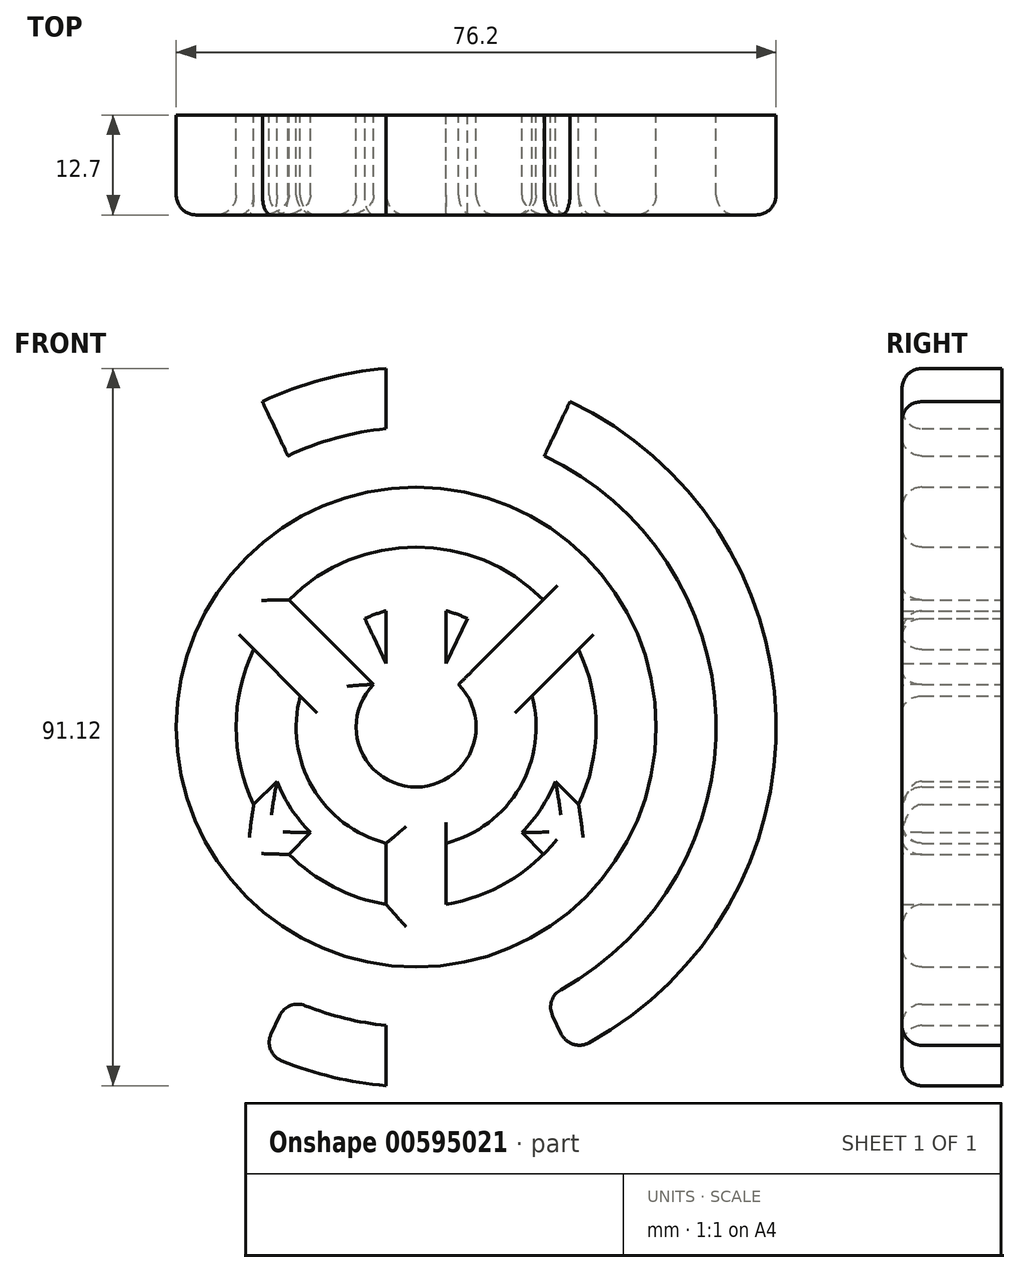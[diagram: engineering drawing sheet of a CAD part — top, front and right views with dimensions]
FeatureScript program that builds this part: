
annotation { "Feature Type Name" : "Feature", "Feature Type Description" : "" }
export const myFeature = defineFeature(function(context is Context, id is Id, definition is map)
    precondition{}
    {
        {
            var Q0;
            Q0=qCreatedBy(makeId("Front.planeOp"),FACE);
            var sketch = newSketch(context, id + "F0", { "sketchPlane" : qUnion([Q0])});
            skCircle(sketch, "E0", {"center": v(0, 0) * mm, "radius": 45.72 * mm});
            skCircle(sketch, "E1", {"center": v(0, 0) * mm, "radius": 38.1 * mm});
            skCircle(sketch, "E2", {"center": v(0, 0) * mm, "radius": 15.24 * mm});
            skCircle(sketch, "E3", {"center": v(0, 0) * mm, "radius": 7.62 * mm});
            skCircle(sketch, "E4", {"center": v(0, 0) * mm, "radius": 30.48 * mm});
            skCircle(sketch, "E5", {"center": v(0, 0) * mm, "radius": 22.86 * mm});
            skLineSegment(sketch, "E6", {"start": v(0, 0) * mm, "end": v(0, -45.72) * mm, "construction": true});
            skLineSegment(sketch, "E7", {"start": v(0, -45.72) * mm, "end": v(0, 45.72) * mm, "construction": true});
            skLineSegment(sketch, "E8", {"start": v(0, 0) * mm, "end": v(-45.72, 0) * mm});
            skLineSegment(sketch, "E9", {"start": v(-45.72, 0) * mm, "end": v(45.72, 0) * mm});
            skLineSegment(sketch, "E10", {"start": v(3.8, 45.56) * mm, "end": v(3.81, -45.56) * mm});
            skLineSegment(sketch, "E11", {"start": v(3.81, -45.56) * mm, "end": v(3.8, 45.56) * mm});
            skLineSegment(sketch, "E12", {"start": v(-3.81, 45.56) * mm, "end": v(-3.8, -45.56) * mm});
            skLineSegment(sketch, "E13", {"start": v(0, 0) * mm, "end": v(19.54, 41.34) * mm});
            skLineSegment(sketch, "E14", {"start": v(19.54, 41.34) * mm, "end": v(-19.54, -41.34) * mm});
            skLineSegment(sketch, "E15.MirrorCS", {"start": v(0, 0) * mm, "end": v(-19.54, 41.34) * mm});
            skLineSegment(sketch, "E16.MirrorCS", {"start": v(-19.54, 41.34) * mm, "end": v(19.54, -41.34) * mm});
            skLineSegment(sketch, "E17", {"start": v(0, 0) * mm, "end": v(21.55, 21.55) * mm});
            skLineSegment(sketch, "E18", {"start": v(21.55, 21.55) * mm, "end": v(0, 0) * mm});
            skLineSegment(sketch, "E19", {"start": v(26.26, 15.48) * mm, "end": v(10.78, 0) * mm});
            skPoint(sketch, "E19.endSnap0", {"position": v(3.8, 0) * mm});
            skLineSegment(sketch, "E20", {"start": v(10.78, 0) * mm, "end": v(26.26, -15.48) * mm});
            skLineSegment(sketch, "E21", {"start": v(0, 0) * mm, "end": v(21.55, -21.55) * mm});
            skLineSegment(sketch, "E22.MirrorCS", {"start": v(0, 0) * mm, "end": v(-21.55, -21.55) * mm});
            skLineSegment(sketch, "E23.MirrorCS", {"start": v(-10.78, 0) * mm, "end": v(-26.26, -15.48) * mm});
            skLineSegment(sketch, "E24.MirrorCS", {"start": v(-21.55, 21.55) * mm, "end": v(0, 0) * mm});
            skLineSegment(sketch, "E25.MirrorCS", {"start": v(-26.26, 15.48) * mm, "end": v(-10.78, 0) * mm});
            skCircle(sketch, "E26", {"center": v(0, 0) * mm, "radius": 18.97 * mm});
            skSolve(sketch);
        }
        {
            var Q0;
            {var subQ0=sQuery(id+"F0.wireOp",EDGE,"E19");var subQ1=sQuery(id+"F0.wireOp",EDGE,"E5");var subQ2=makeQuery(id+"F0.imprint","INTERSECT",VERTEX,{"derivedFrom":[subQ1,subQ0]});Q0=makeQuery(id+"F0.imprint","IMPRINT",FACE,{"disambiguationData":[TD([[makeQuery(id+"F0.imprint","IMPRINT",EDGE,{"disambiguationData":[TD([[subQ2,-1.0]])],"derivedFrom":subQ1}),1.0]])]});}
            var Q1;
            {var subQ0=sQuery(id+"F0.wireOp",EDGE,"E23.MirrorCS");var subQ1=sQuery(id+"F0.wireOp",EDGE,"E5");var subQ2=makeQuery(id+"F0.imprint","INTERSECT",VERTEX,{"derivedFrom":[subQ1,subQ0]});Q1=makeQuery(id+"F0.imprint","IMPRINT",FACE,{"disambiguationData":[TD([[makeQuery(id+"F0.imprint","IMPRINT",EDGE,{"disambiguationData":[TD([[subQ2,-1.0]])],"derivedFrom":subQ1}),1.0]])]});}
            var Q2;
            {var subQ3=sQuery(id+"F0.wireOp",EDGE,"E2");var subQ7=sQuery(id+"F0.wireOp",EDGE,"E21");var subQ9=makeQuery(id+"F0.imprint","INTERSECT",VERTEX,{"derivedFrom":[subQ3,subQ7]});Q2=makeQuery(id+"F0.imprint","IMPRINT",FACE,{"disambiguationData":[TD([[makeQuery(id+"F0.imprint","IMPRINT",EDGE,{"disambiguationData":[TD([[subQ9,-1.0]])],"derivedFrom":subQ3}),1.0]])]});}
            var Q3;
            {var subQ0=sQuery(id+"F0.wireOp",EDGE,"E12");var subQ1=sQuery(id+"F0.wireOp",EDGE,"E3");var subQ2=makeQuery(id+"F0.imprint","INTERSECT",VERTEX,{"disambiguationData":[OD(1.0)],"derivedFrom":[subQ1,subQ0]});Q3=makeQuery(id+"F0.imprint","IMPRINT",FACE,{"disambiguationData":[TD([[makeQuery(id+"F0.imprint","IMPRINT",EDGE,{"disambiguationData":[TD([[subQ2,-1.0]])],"derivedFrom":subQ1}),-1.0]])]});}
            var Q4;
            {var subQ0=sQuery(id+"F0.wireOp",EDGE,"E9");var subQ1=sQuery(id+"F0.wireOp",EDGE,"E0");var subQ2=makeQuery(id+"F0.imprint","INTERSECT",VERTEX,{"disambiguationData":[OD(0.0)],"derivedFrom":[subQ1,subQ0]});Q4=makeQuery(id+"F0.imprint","IMPRINT",FACE,{"disambiguationData":[TD([[makeQuery(id+"F0.imprint","IMPRINT",EDGE,{"disambiguationData":[TD([[subQ2,1.0]])],"derivedFrom":subQ1}),1.0]])]});}
            var Q5;
            {var subQ0=sQuery(id+"F0.wireOp",EDGE,"E11");var subQ1=sQuery(id+"F0.wireOp",EDGE,"E0");var subQ2=makeQuery(id+"F0.imprint","INTERSECT",VERTEX,{"disambiguationData":[OD(0.0)],"derivedFrom":[subQ1,subQ0]});Q5=makeQuery(id+"F0.imprint","IMPRINT",FACE,{"disambiguationData":[TD([[makeQuery(id+"F0.imprint","IMPRINT",EDGE,{"disambiguationData":[TD([[subQ2,1.0]])],"derivedFrom":subQ1}),1.0]])]});}
            var Q6;
            {var subQ0=sQuery(id+"F0.wireOp",EDGE,"E9");var subQ1=sQuery(id+"F0.wireOp",EDGE,"E0");var subQ2=makeQuery(id+"F0.imprint","INTERSECT",VERTEX,{"disambiguationData":[OD(1.0)],"derivedFrom":[subQ1,subQ0]});Q6=makeQuery(id+"F0.imprint","IMPRINT",FACE,{"disambiguationData":[TD([[makeQuery(id+"F0.imprint","IMPRINT",EDGE,{"disambiguationData":[TD([[subQ2,-1.0]])],"derivedFrom":subQ1}),1.0]])]});}
            var Q7;
            {var subQ0=sQuery(id+"F0.wireOp",EDGE,"E25.MirrorCS");var subQ1=sQuery(id+"F0.wireOp",EDGE,"E2");var subQ2=makeQuery(id+"F0.imprint","INTERSECT",VERTEX,{"derivedFrom":[subQ1,subQ0]});Q7=makeQuery(id+"F0.imprint","IMPRINT",FACE,{"disambiguationData":[TD([[makeQuery(id+"F0.imprint","IMPRINT",EDGE,{"disambiguationData":[TD([[subQ2,-1.0]])],"derivedFrom":subQ1}),1.0]])]});}
            var Q8;
            {var subQ0=sQuery(id+"F0.wireOp",EDGE,"E9");var subQ1=sQuery(id+"F0.wireOp",EDGE,"E0");var subQ2=makeQuery(id+"F0.imprint","INTERSECT",VERTEX,{"disambiguationData":[OD(1.0)],"derivedFrom":[subQ1,subQ0]});Q8=makeQuery(id+"F0.imprint","IMPRINT",FACE,{"disambiguationData":[TD([[makeQuery(id+"F0.imprint","IMPRINT",EDGE,{"disambiguationData":[TD([[subQ2,1.0]])],"derivedFrom":subQ1}),1.0]])]});}
            var Q9;
            {var subQ0=sQuery(id+"F0.wireOp",EDGE,"E12");var subQ1=sQuery(id+"F0.wireOp",EDGE,"E4");var subQ2=makeQuery(id+"F0.imprint","INTERSECT",VERTEX,{"disambiguationData":[OD(0.0)],"derivedFrom":[subQ1,subQ0]});Q9=makeQuery(id+"F0.imprint","IMPRINT",FACE,{"disambiguationData":[TD([[makeQuery(id+"F0.imprint","IMPRINT",EDGE,{"disambiguationData":[TD([[subQ2,-1.0]])],"derivedFrom":subQ1}),1.0]])]});}
            var Q10;
            {var subQ0=sQuery(id+"F0.wireOp",EDGE,"E24.MirrorCS");var subQ1=sQuery(id+"F0.wireOp",EDGE,"E5");var subQ2=makeQuery(id+"F0.imprint","INTERSECT",VERTEX,{"derivedFrom":[subQ1,subQ0]});Q10=makeQuery(id+"F0.imprint","IMPRINT",FACE,{"disambiguationData":[TD([[makeQuery(id+"F0.imprint","IMPRINT",EDGE,{"disambiguationData":[TD([[subQ2,-1.0]])],"derivedFrom":subQ1}),1.0]])]});}
            var Q11;
            {var subQ0=sQuery(id+"F0.wireOp",EDGE,"E23.MirrorCS");var subQ1=sQuery(id+"F0.wireOp",EDGE,"E4");var subQ2=makeQuery(id+"F0.imprint","INTERSECT",VERTEX,{"derivedFrom":[subQ1,subQ0]});Q11=makeQuery(id+"F0.imprint","IMPRINT",FACE,{"disambiguationData":[TD([[makeQuery(id+"F0.imprint","IMPRINT",EDGE,{"disambiguationData":[TD([[subQ2,1.0]])],"derivedFrom":subQ1}),1.0]])]});}
            var Q12;
            {var subQ0=sQuery(id+"F0.wireOp",EDGE,"E11");var subQ1=sQuery(id+"F0.wireOp",EDGE,"E2");var subQ2=makeQuery(id+"F0.imprint","INTERSECT",VERTEX,{"disambiguationData":[OD(0.0)],"derivedFrom":[subQ1,subQ0]});Q12=makeQuery(id+"F0.imprint","IMPRINT",FACE,{"disambiguationData":[TD([[makeQuery(id+"F0.imprint","IMPRINT",EDGE,{"disambiguationData":[TD([[subQ2,-1.0]])],"derivedFrom":subQ1}),-1.0]])]});}
            var Q13;
            {var subQ0=sQuery(id+"F0.wireOp",EDGE,"E25.MirrorCS");var subQ1=sQuery(id+"F0.wireOp",EDGE,"E4");var subQ2=makeQuery(id+"F0.imprint","INTERSECT",VERTEX,{"derivedFrom":[subQ1,subQ0]});Q13=makeQuery(id+"F0.imprint","IMPRINT",FACE,{"disambiguationData":[TD([[makeQuery(id+"F0.imprint","IMPRINT",EDGE,{"disambiguationData":[TD([[subQ2,-1.0]])],"derivedFrom":subQ1}),1.0]])]});}
            var Q14;
            {var subQ0=sQuery(id+"F0.wireOp",EDGE,"E11");var subQ1=sQuery(id+"F0.wireOp",EDGE,"E4");var subQ2=makeQuery(id+"F0.imprint","INTERSECT",VERTEX,{"disambiguationData":[OD(1.0)],"derivedFrom":[subQ1,subQ0]});Q14=makeQuery(id+"F0.imprint","IMPRINT",FACE,{"disambiguationData":[TD([[makeQuery(id+"F0.imprint","IMPRINT",EDGE,{"disambiguationData":[TD([[subQ2,-1.0]])],"derivedFrom":subQ1}),1.0]])]});}
            var Q15;
            {var subQ0=sQuery(id+"F0.wireOp",EDGE,"E21");var subQ1=sQuery(id+"F0.wireOp",EDGE,"E5");var subQ2=makeQuery(id+"F0.imprint","INTERSECT",VERTEX,{"derivedFrom":[subQ1,subQ0]});Q15=makeQuery(id+"F0.imprint","IMPRINT",FACE,{"disambiguationData":[TD([[makeQuery(id+"F0.imprint","IMPRINT",EDGE,{"disambiguationData":[TD([[subQ2,-1.0]])],"derivedFrom":subQ1}),1.0]])]});}
            var Q16;
            {var subQ0=sQuery(id+"F0.wireOp",EDGE,"E20");var subQ1=sQuery(id+"F0.wireOp",EDGE,"E4");var subQ2=makeQuery(id+"F0.imprint","INTERSECT",VERTEX,{"derivedFrom":[subQ1,subQ0]});Q16=makeQuery(id+"F0.imprint","IMPRINT",FACE,{"disambiguationData":[TD([[makeQuery(id+"F0.imprint","IMPRINT",EDGE,{"disambiguationData":[TD([[subQ2,-1.0]])],"derivedFrom":subQ1}),1.0]])]});}
            var Q17;
            {var subQ0=sQuery(id+"F0.wireOp",EDGE,"E12");var subQ1=sQuery(id+"F0.wireOp",EDGE,"E2");var subQ2=makeQuery(id+"F0.imprint","INTERSECT",VERTEX,{"disambiguationData":[OD(1.0)],"derivedFrom":[subQ1,subQ0]});Q17=makeQuery(id+"F0.imprint","IMPRINT",FACE,{"disambiguationData":[TD([[makeQuery(id+"F0.imprint","IMPRINT",EDGE,{"disambiguationData":[TD([[subQ2,-1.0]])],"derivedFrom":subQ1}),1.0]])]});}
            var Q18;
            {var subQ0=sQuery(id+"F0.wireOp",EDGE,"E12");var subQ1=sQuery(id+"F0.wireOp",EDGE,"E4");var subQ2=makeQuery(id+"F0.imprint","INTERSECT",VERTEX,{"disambiguationData":[OD(1.0)],"derivedFrom":[subQ1,subQ0]});Q18=makeQuery(id+"F0.imprint","IMPRINT",FACE,{"disambiguationData":[TD([[makeQuery(id+"F0.imprint","IMPRINT",EDGE,{"disambiguationData":[TD([[subQ2,-1.0]])],"derivedFrom":subQ1}),1.0]])]});}
            var Q19;
            {var subQ0=sQuery(id+"F0.wireOp",EDGE,"E11");var subQ1=sQuery(id+"F0.wireOp",EDGE,"E0");var subQ2=makeQuery(id+"F0.imprint","INTERSECT",VERTEX,{"disambiguationData":[OD(1.0)],"derivedFrom":[subQ1,subQ0]});Q19=makeQuery(id+"F0.imprint","IMPRINT",FACE,{"disambiguationData":[TD([[makeQuery(id+"F0.imprint","IMPRINT",EDGE,{"disambiguationData":[TD([[subQ2,-1.0]])],"derivedFrom":subQ1}),1.0]])]});}
            var Q20;
            {var subQ1=sQuery(id+"F0.wireOp",EDGE,"E2");var subQ5=sQuery(id+"F0.wireOp",EDGE,"E19");var subQ9=makeQuery(id+"F0.imprint","INTERSECT",VERTEX,{"derivedFrom":[subQ1,subQ5]});Q20=makeQuery(id+"F0.imprint","IMPRINT",FACE,{"disambiguationData":[TD([[makeQuery(id+"F0.imprint","IMPRINT",EDGE,{"disambiguationData":[TD([[subQ9,-1.0]])],"derivedFrom":subQ1}),1.0]])]});}
            var Q21;
            {var subQ0=sQuery(id+"F0.wireOp",EDGE,"E14");var subQ1=sQuery(id+"F0.wireOp",EDGE,"E2");var subQ2=makeQuery(id+"F0.imprint","INTERSECT",VERTEX,{"disambiguationData":[OD(0.0)],"derivedFrom":[subQ1,subQ0]});Q21=makeQuery(id+"F0.imprint","IMPRINT",FACE,{"disambiguationData":[TD([[makeQuery(id+"F0.imprint","IMPRINT",EDGE,{"disambiguationData":[TD([[subQ2,-1.0]])],"derivedFrom":subQ1}),1.0]])]});}
            var Q22;
            {var subQ0=sQuery(id+"F0.wireOp",EDGE,"E16.MirrorCS");var subQ1=sQuery(id+"F0.wireOp",EDGE,"E2");var subQ2=makeQuery(id+"F0.imprint","INTERSECT",VERTEX,{"disambiguationData":[OD(1.0)],"derivedFrom":[subQ1,subQ0]});Q22=makeQuery(id+"F0.imprint","IMPRINT",FACE,{"disambiguationData":[TD([[makeQuery(id+"F0.imprint","IMPRINT",EDGE,{"disambiguationData":[TD([[subQ2,-1.0]])],"derivedFrom":subQ1}),1.0]])]});}
            var Q23;
            {var subQ0=sQuery(id+"F0.wireOp",EDGE,"E18");var subQ6=sQuery(id+"F0.wireOp",EDGE,"E2");var subQ9=makeQuery(id+"F0.imprint","INTERSECT",VERTEX,{"derivedFrom":[subQ6,subQ0]});Q23=makeQuery(id+"F0.imprint","IMPRINT",FACE,{"disambiguationData":[TD([[makeQuery(id+"F0.imprint","IMPRINT",EDGE,{"disambiguationData":[TD([[subQ9,-1.0]])],"derivedFrom":subQ6}),1.0]])]});}
            var Q24;
            {var subQ0=sQuery(id+"F0.wireOp",EDGE,"E9");var subQ1=sQuery(id+"F0.wireOp",EDGE,"E2");var subQ2=makeQuery(id+"F0.imprint","INTERSECT",VERTEX,{"disambiguationData":[OD(1.0)],"derivedFrom":[subQ1,subQ0]});Q24=makeQuery(id+"F0.imprint","IMPRINT",FACE,{"disambiguationData":[TD([[makeQuery(id+"F0.imprint","IMPRINT",EDGE,{"disambiguationData":[TD([[subQ2,-1.0]])],"derivedFrom":subQ1}),1.0]])]});}
            var Q25;
            {var subQ0=sQuery(id+"F0.wireOp",EDGE,"E11");var subQ1=sQuery(id+"F0.wireOp",EDGE,"E3");var subQ2=makeQuery(id+"F0.imprint","INTERSECT",VERTEX,{"disambiguationData":[OD(0.0)],"derivedFrom":[subQ1,subQ0]});Q25=makeQuery(id+"F0.imprint","IMPRINT",FACE,{"disambiguationData":[TD([[makeQuery(id+"F0.imprint","IMPRINT",EDGE,{"disambiguationData":[TD([[subQ2,-1.0]])],"derivedFrom":subQ1}),-1.0]])]});}
            var Q26;
            {var subQ0=sQuery(id+"F0.wireOp",EDGE,"E16.MirrorCS");var subQ1=sQuery(id+"F0.wireOp",EDGE,"E3");var subQ2=makeQuery(id+"F0.imprint","INTERSECT",VERTEX,{"disambiguationData":[OD(0.0)],"derivedFrom":[subQ1,subQ0]});Q26=makeQuery(id+"F0.imprint","IMPRINT",FACE,{"disambiguationData":[TD([[makeQuery(id+"F0.imprint","IMPRINT",EDGE,{"disambiguationData":[TD([[subQ2,-1.0]])],"derivedFrom":subQ1}),-1.0]])]});}
            var Q27;
            {var subQ0=sQuery(id+"F0.wireOp",EDGE,"E18");var subQ1=sQuery(id+"F0.wireOp",EDGE,"E4");var subQ2=makeQuery(id+"F0.imprint","INTERSECT",VERTEX,{"derivedFrom":[subQ1,subQ0]});Q27=makeQuery(id+"F0.imprint","IMPRINT",FACE,{"disambiguationData":[TD([[makeQuery(id+"F0.imprint","IMPRINT",EDGE,{"disambiguationData":[TD([[subQ2,1.0]])],"derivedFrom":subQ1}),1.0]])]});}
            var Q28;
            {var subQ0=sQuery(id+"F0.wireOp",EDGE,"E11");var subQ1=sQuery(id+"F0.wireOp",EDGE,"E2");var subQ2=makeQuery(id+"F0.imprint","INTERSECT",VERTEX,{"disambiguationData":[OD(1.0)],"derivedFrom":[subQ1,subQ0]});Q28=makeQuery(id+"F0.imprint","IMPRINT",FACE,{"disambiguationData":[TD([[makeQuery(id+"F0.imprint","IMPRINT",EDGE,{"disambiguationData":[TD([[subQ2,-1.0]])],"derivedFrom":subQ1}),1.0]])]});}
            var Q29;
            {var subQ0=sQuery(id+"F0.wireOp",EDGE,"E20");var subQ1=sQuery(id+"F0.wireOp",EDGE,"E4");var subQ2=makeQuery(id+"F0.imprint","INTERSECT",VERTEX,{"derivedFrom":[subQ1,subQ0]});Q29=makeQuery(id+"F0.imprint","IMPRINT",FACE,{"disambiguationData":[TD([[makeQuery(id+"F0.imprint","IMPRINT",EDGE,{"disambiguationData":[TD([[subQ2,1.0]])],"derivedFrom":subQ1}),1.0]])]});}
            var Q30;
            {var subQ0=sQuery(id+"F0.wireOp",EDGE,"E12");var subQ1=sQuery(id+"F0.wireOp",EDGE,"E2");var subQ2=makeQuery(id+"F0.imprint","INTERSECT",VERTEX,{"disambiguationData":[OD(1.0)],"derivedFrom":[subQ1,subQ0]});Q30=makeQuery(id+"F0.imprint","IMPRINT",FACE,{"disambiguationData":[TD([[makeQuery(id+"F0.imprint","IMPRINT",EDGE,{"disambiguationData":[TD([[subQ2,-1.0]])],"derivedFrom":subQ1}),-1.0]])]});}
            var Q31;
            {var subQ0=sQuery(id+"F0.wireOp",EDGE,"E11");var subQ1=sQuery(id+"F0.wireOp",EDGE,"E4");var subQ2=makeQuery(id+"F0.imprint","INTERSECT",VERTEX,{"disambiguationData":[OD(0.0)],"derivedFrom":[subQ1,subQ0]});Q31=makeQuery(id+"F0.imprint","IMPRINT",FACE,{"disambiguationData":[TD([[makeQuery(id+"F0.imprint","IMPRINT",EDGE,{"disambiguationData":[TD([[subQ2,-1.0]])],"derivedFrom":subQ1}),1.0]])]});}
            var Q32;
            {var subQ0=sQuery(id+"F0.wireOp",EDGE,"E9");var subQ1=sQuery(id+"F0.wireOp",EDGE,"E0");var subQ2=makeQuery(id+"F0.imprint","INTERSECT",VERTEX,{"disambiguationData":[OD(0.0)],"derivedFrom":[subQ1,subQ0]});Q32=makeQuery(id+"F0.imprint","IMPRINT",FACE,{"disambiguationData":[TD([[makeQuery(id+"F0.imprint","IMPRINT",EDGE,{"disambiguationData":[TD([[subQ2,-1.0]])],"derivedFrom":subQ1}),1.0]])]});}
            var Q33;
            {var subQ0=sQuery(id+"F0.wireOp",EDGE,"E16.MirrorCS");var subQ1=sQuery(id+"F0.wireOp",EDGE,"E3");var subQ2=makeQuery(id+"F0.imprint","INTERSECT",VERTEX,{"disambiguationData":[OD(1.0)],"derivedFrom":[subQ1,subQ0]});Q33=makeQuery(id+"F0.imprint","IMPRINT",FACE,{"disambiguationData":[TD([[makeQuery(id+"F0.imprint","IMPRINT",EDGE,{"disambiguationData":[TD([[subQ2,-1.0]])],"derivedFrom":subQ1}),-1.0]])]});}
            var Q34;
            {var subQ0=sQuery(id+"F0.wireOp",EDGE,"E19");var subQ1=sQuery(id+"F0.wireOp",EDGE,"E2");var subQ2=makeQuery(id+"F0.imprint","INTERSECT",VERTEX,{"derivedFrom":[subQ1,subQ0]});Q34=makeQuery(id+"F0.imprint","IMPRINT",FACE,{"disambiguationData":[TD([[makeQuery(id+"F0.imprint","IMPRINT",EDGE,{"disambiguationData":[TD([[subQ2,-1.0]])],"derivedFrom":subQ1}),-1.0]])]});}
            var Q35;
            {var subQ5=sQuery(id+"F0.wireOp",EDGE,"E24.MirrorCS");var subQ7=sQuery(id+"F0.wireOp",EDGE,"E2");var subQ8=makeQuery(id+"F0.imprint","INTERSECT",VERTEX,{"derivedFrom":[subQ7,subQ5]});Q35=makeQuery(id+"F0.imprint","IMPRINT",FACE,{"disambiguationData":[TD([[makeQuery(id+"F0.imprint","IMPRINT",EDGE,{"disambiguationData":[TD([[subQ8,-1.0]])],"derivedFrom":subQ7}),1.0]])]});}
            var Q36;
            {var subQ0=sQuery(id+"F0.wireOp",EDGE,"E12");var subQ1=sQuery(id+"F0.wireOp",EDGE,"E5");var subQ2=makeQuery(id+"F0.imprint","INTERSECT",VERTEX,{"disambiguationData":[OD(1.0)],"derivedFrom":[subQ1,subQ0]});Q36=makeQuery(id+"F0.imprint","IMPRINT",FACE,{"disambiguationData":[TD([[makeQuery(id+"F0.imprint","IMPRINT",EDGE,{"disambiguationData":[TD([[subQ2,-1.0]])],"derivedFrom":subQ1}),1.0]])]});}
            var Q37;
            {var subQ0=sQuery(id+"F0.wireOp",EDGE,"E14");var subQ1=sQuery(id+"F0.wireOp",EDGE,"E4");var subQ2=makeQuery(id+"F0.imprint","INTERSECT",VERTEX,{"disambiguationData":[OD(1.0)],"derivedFrom":[subQ1,subQ0]});Q37=makeQuery(id+"F0.imprint","IMPRINT",FACE,{"disambiguationData":[TD([[makeQuery(id+"F0.imprint","IMPRINT",EDGE,{"disambiguationData":[TD([[subQ2,-1.0]])],"derivedFrom":subQ1}),1.0]])]});}
            var Q38;
            {var subQ0=sQuery(id+"F0.wireOp",EDGE,"E11");var subQ1=sQuery(id+"F0.wireOp",EDGE,"E5");var subQ2=makeQuery(id+"F0.imprint","INTERSECT",VERTEX,{"disambiguationData":[OD(0.0)],"derivedFrom":[subQ1,subQ0]});Q38=makeQuery(id+"F0.imprint","IMPRINT",FACE,{"disambiguationData":[TD([[makeQuery(id+"F0.imprint","IMPRINT",EDGE,{"disambiguationData":[TD([[subQ2,-1.0]])],"derivedFrom":subQ1}),1.0]])]});}
            var Q39;
            {var subQ0=sQuery(id+"F0.wireOp",EDGE,"E11");var subQ1=sQuery(id+"F0.wireOp",EDGE,"E2");var subQ2=makeQuery(id+"F0.imprint","INTERSECT",VERTEX,{"disambiguationData":[OD(0.0)],"derivedFrom":[subQ1,subQ0]});Q39=makeQuery(id+"F0.imprint","IMPRINT",FACE,{"disambiguationData":[TD([[makeQuery(id+"F0.imprint","IMPRINT",EDGE,{"disambiguationData":[TD([[subQ2,-1.0]])],"derivedFrom":subQ1}),1.0]])]});}
            var Q40;
            {var subQ0=sQuery(id+"F0.wireOp",EDGE,"E12");var subQ1=sQuery(id+"F0.wireOp",EDGE,"E2");var subQ2=makeQuery(id+"F0.imprint","INTERSECT",VERTEX,{"disambiguationData":[OD(0.0)],"derivedFrom":[subQ1,subQ0]});Q40=makeQuery(id+"F0.imprint","IMPRINT",FACE,{"disambiguationData":[TD([[makeQuery(id+"F0.imprint","IMPRINT",EDGE,{"disambiguationData":[TD([[subQ2,-1.0]])],"derivedFrom":subQ1}),1.0]])]});}
            var Q41;
            {var subQ3=sQuery(id+"F0.wireOp",EDGE,"E16.MirrorCS");var subQ5=sQuery(id+"F0.wireOp",EDGE,"E2");var subQ6=makeQuery(id+"F0.imprint","INTERSECT",VERTEX,{"disambiguationData":[OD(0.0)],"derivedFrom":[subQ5,subQ3]});Q41=makeQuery(id+"F0.imprint","IMPRINT",FACE,{"disambiguationData":[TD([[makeQuery(id+"F0.imprint","IMPRINT",EDGE,{"disambiguationData":[TD([[subQ6,-1.0]])],"derivedFrom":subQ5}),1.0]])]});}
            var Q42;
            {var subQ0=sQuery(id+"F0.wireOp",EDGE,"E19");var subQ1=sQuery(id+"F0.wireOp",EDGE,"E4");var subQ2=makeQuery(id+"F0.imprint","INTERSECT",VERTEX,{"derivedFrom":[subQ1,subQ0]});Q42=makeQuery(id+"F0.imprint","IMPRINT",FACE,{"disambiguationData":[TD([[makeQuery(id+"F0.imprint","IMPRINT",EDGE,{"disambiguationData":[TD([[subQ2,1.0]])],"derivedFrom":subQ1}),1.0]])]});}
            var Q43;
            {var subQ0=sQuery(id+"F0.wireOp",EDGE,"E22.MirrorCS");var subQ1=sQuery(id+"F0.wireOp",EDGE,"E4");var subQ2=makeQuery(id+"F0.imprint","INTERSECT",VERTEX,{"derivedFrom":[subQ1,subQ0]});Q43=makeQuery(id+"F0.imprint","IMPRINT",FACE,{"disambiguationData":[TD([[makeQuery(id+"F0.imprint","IMPRINT",EDGE,{"disambiguationData":[TD([[subQ2,1.0]])],"derivedFrom":subQ1}),1.0]])]});}
            var Q44;
            {var subQ1=sQuery(id+"F0.wireOp",EDGE,"E2");var subQ5=sQuery(id+"F0.wireOp",EDGE,"E23.MirrorCS");var subQ9=makeQuery(id+"F0.imprint","INTERSECT",VERTEX,{"derivedFrom":[subQ1,subQ5]});Q44=makeQuery(id+"F0.imprint","IMPRINT",FACE,{"disambiguationData":[TD([[makeQuery(id+"F0.imprint","IMPRINT",EDGE,{"disambiguationData":[TD([[subQ9,-1.0]])],"derivedFrom":subQ1}),1.0]])]});}
            var Q45;
            {var subQ0=sQuery(id+"F0.wireOp",EDGE,"E24.MirrorCS");var subQ1=sQuery(id+"F0.wireOp",EDGE,"E4");var subQ2=makeQuery(id+"F0.imprint","INTERSECT",VERTEX,{"derivedFrom":[subQ1,subQ0]});Q45=makeQuery(id+"F0.imprint","IMPRINT",FACE,{"disambiguationData":[TD([[makeQuery(id+"F0.imprint","IMPRINT",EDGE,{"disambiguationData":[TD([[subQ2,-1.0]])],"derivedFrom":subQ1}),1.0]])]});}
            var Q46;
            {var subQ0=sQuery(id+"F0.wireOp",EDGE,"E24.MirrorCS");var subQ1=sQuery(id+"F0.wireOp",EDGE,"E2");var subQ2=makeQuery(id+"F0.imprint","INTERSECT",VERTEX,{"derivedFrom":[subQ1,subQ0]});Q46=makeQuery(id+"F0.imprint","IMPRINT",FACE,{"disambiguationData":[TD([[makeQuery(id+"F0.imprint","IMPRINT",EDGE,{"disambiguationData":[TD([[subQ2,-1.0]])],"derivedFrom":subQ1}),-1.0]])]});}
            var Q47;
            {var subQ1=sQuery(id+"F0.wireOp",EDGE,"E2");var subQ5=sQuery(id+"F0.wireOp",EDGE,"E22.MirrorCS");var subQ6=makeQuery(id+"F0.imprint","INTERSECT",VERTEX,{"derivedFrom":[subQ1,subQ5]});Q47=makeQuery(id+"F0.imprint","IMPRINT",FACE,{"disambiguationData":[TD([[makeQuery(id+"F0.imprint","IMPRINT",EDGE,{"disambiguationData":[TD([[subQ6,-1.0]])],"derivedFrom":subQ1}),1.0]])]});}
            var Q48;
            {var subQ0=sQuery(id+"F0.wireOp",EDGE,"E9");var subQ1=sQuery(id+"F0.wireOp",EDGE,"E2");var subQ2=makeQuery(id+"F0.imprint","INTERSECT",VERTEX,{"disambiguationData":[OD(0.0)],"derivedFrom":[subQ1,subQ0]});Q48=makeQuery(id+"F0.imprint","IMPRINT",FACE,{"disambiguationData":[TD([[makeQuery(id+"F0.imprint","IMPRINT",EDGE,{"disambiguationData":[TD([[subQ2,1.0]])],"derivedFrom":subQ1}),1.0]])]});}
            var Q49;
            {var subQ0=sQuery(id+"F0.wireOp",EDGE,"E11");var subQ1=sQuery(id+"F0.wireOp",EDGE,"E0");var subQ2=makeQuery(id+"F0.imprint","INTERSECT",VERTEX,{"disambiguationData":[OD(0.0)],"derivedFrom":[subQ1,subQ0]});Q49=makeQuery(id+"F0.imprint","IMPRINT",FACE,{"disambiguationData":[TD([[makeQuery(id+"F0.imprint","IMPRINT",EDGE,{"disambiguationData":[TD([[subQ2,-1.0]])],"derivedFrom":subQ1}),1.0]])]});}
            var Q50;
            {var subQ0=sQuery(id+"F0.wireOp",EDGE,"E11");var subQ1=sQuery(id+"F0.wireOp",EDGE,"E0");var subQ2=makeQuery(id+"F0.imprint","INTERSECT",VERTEX,{"disambiguationData":[OD(1.0)],"derivedFrom":[subQ1,subQ0]});Q50=makeQuery(id+"F0.imprint","IMPRINT",FACE,{"disambiguationData":[TD([[makeQuery(id+"F0.imprint","IMPRINT",EDGE,{"disambiguationData":[TD([[subQ2,1.0]])],"derivedFrom":subQ1}),1.0]])]});}
            var Q51;
            {var subQ0=sQuery(id+"F0.wireOp",EDGE,"E19");var subQ1=sQuery(id+"F0.wireOp",EDGE,"E2");var subQ2=makeQuery(id+"F0.imprint","INTERSECT",VERTEX,{"derivedFrom":[subQ1,subQ0]});Q51=makeQuery(id+"F0.imprint","IMPRINT",FACE,{"disambiguationData":[TD([[makeQuery(id+"F0.imprint","IMPRINT",EDGE,{"disambiguationData":[TD([[subQ2,1.0]])],"derivedFrom":subQ1}),1.0]])]});}
            var Q52;
            {var subQ0=sQuery(id+"F0.wireOp",EDGE,"E12");var subQ1=sQuery(id+"F0.wireOp",EDGE,"E0");var subQ2=makeQuery(id+"F0.imprint","INTERSECT",VERTEX,{"disambiguationData":[OD(0.0)],"derivedFrom":[subQ1,subQ0]});Q52=makeQuery(id+"F0.imprint","IMPRINT",FACE,{"disambiguationData":[TD([[makeQuery(id+"F0.imprint","IMPRINT",EDGE,{"disambiguationData":[TD([[subQ2,-1.0]])],"derivedFrom":subQ1}),1.0]])]});}
            var Q53;
            {var subQ0=sQuery(id+"F0.wireOp",EDGE,"E12");var subQ1=sQuery(id+"F0.wireOp",EDGE,"E0");var subQ2=makeQuery(id+"F0.imprint","INTERSECT",VERTEX,{"disambiguationData":[OD(1.0)],"derivedFrom":[subQ1,subQ0]});Q53=makeQuery(id+"F0.imprint","IMPRINT",FACE,{"disambiguationData":[TD([[makeQuery(id+"F0.imprint","IMPRINT",EDGE,{"disambiguationData":[TD([[subQ2,1.0]])],"derivedFrom":subQ1}),1.0]])]});}
            var Q54;
            {var subQ0=sQuery(id+"F0.wireOp",EDGE,"E14");var subQ1=sQuery(id+"F0.wireOp",EDGE,"E4");var subQ2=makeQuery(id+"F0.imprint","INTERSECT",VERTEX,{"disambiguationData":[OD(0.0)],"derivedFrom":[subQ1,subQ0]});Q54=makeQuery(id+"F0.imprint","IMPRINT",FACE,{"disambiguationData":[TD([[makeQuery(id+"F0.imprint","IMPRINT",EDGE,{"disambiguationData":[TD([[subQ2,-1.0]])],"derivedFrom":subQ1}),1.0]])]});}
            var Q55;
            {var subQ0=sQuery(id+"F0.wireOp",EDGE,"E14");var subQ1=sQuery(id+"F0.wireOp",EDGE,"E2");var subQ2=makeQuery(id+"F0.imprint","INTERSECT",VERTEX,{"disambiguationData":[OD(1.0)],"derivedFrom":[subQ1,subQ0]});Q55=makeQuery(id+"F0.imprint","IMPRINT",FACE,{"disambiguationData":[TD([[makeQuery(id+"F0.imprint","IMPRINT",EDGE,{"disambiguationData":[TD([[subQ2,-1.0]])],"derivedFrom":subQ1}),1.0]])]});}
            extrude(context, id + "F1", {"entities" : qUnion([Q0, Q1, Q2, Q3, Q4, Q5, Q6, Q7, Q8, Q9, Q10, Q11, Q12, Q13, Q14, Q15, Q16, Q17, Q18, Q19, Q20, Q21, Q22, Q23, Q24, Q25, Q26, Q27, Q28, Q29, Q30, Q31, Q32, Q33, Q34, Q35, Q36, Q37, Q38, Q39, Q40, Q41, Q42, Q43, Q44, Q45, Q46, Q47, Q48, Q49, Q50, Q51, Q52, Q53, Q54, Q55]), "depth" : 12.7 * mm, "offsetDistance" : 25.4 * mm});
        }
        {
            var Q0;
            Q0=makeQuery(id+"F1.opExtrude","CAP_EDGE",EDGE,{"disambiguationData":[OSD([sQuery(id+"F0.wireOp",EDGE,"E0")])],"isStart":false});
            fillet(context, id + "F2", {"entities" : qUnion([Q0]), "radius" : 2.54 * mm, "tangentPropagation" : true, "allowEdgeOverflow" : false});
        }
        {
            var Q0;
            Q0=makeQuery(id+"F1.opExtrude","CAP_EDGE",EDGE,{"disambiguationData":[OSD([sQuery(id+"F0.wireOp",EDGE,"E1")])],"isStart":false});
            fillet(context, id + "F3", {"entities" : qUnion([Q0]), "radius" : 2.54 * mm, "tangentPropagation" : true, "allowEdgeOverflow" : false});
        }
        {
            var Q0;
            {var subQ0=sQuery(id+"F0.wireOp",EDGE,"E16.MirrorCS");Q0=makeQuery(id+"F1.opExtrude","CAP_EDGE",EDGE,{"disambiguationData":[OSD([subQ0]),TDD([makeQuery(id+"F0.imprint","IMPRINT",EDGE,{"disambiguationData":[TD([[makeQuery(id+"F0.imprint","INTERSECT",VERTEX,{"disambiguationData":[OD(0.0)],"derivedFrom":[sQuery(id+"F0.wireOp",EDGE,"E4"),subQ0]}),-1.0]])],"derivedFrom":subQ0})])],"isStart":false});}
            var Q1;
            {var subQ0=sQuery(id+"F0.wireOp",EDGE,"E4");var subQ1=makeQuery(id+"F0.imprint","INTERSECT",VERTEX,{"derivedFrom":[subQ0,sQuery(id+"F0.wireOp",EDGE,"E20")]});var subQ3=makeQuery(id+"F0.imprint","INTERSECT",VERTEX,{"derivedFrom":[subQ0,sQuery(id+"F0.wireOp",EDGE,"E19")]});Q1=makeQuery(id+"F1.opExtrude","CAP_EDGE",EDGE,{"disambiguationData":[OSD([subQ0]),TDD([makeQuery(id+"F0.imprint","IMPRINT",EDGE,{"disambiguationData":[TD([[subQ3,1.0]])],"derivedFrom":subQ0}),makeQuery(id+"F0.imprint","IMPRINT",EDGE,{"disambiguationData":[TD([[makeQuery(id+"F0.imprint","INTERSECT",VERTEX,{"derivedFrom":[subQ0,sQuery(id+"F0.wireOp",EDGE,"E18")]}),1.0]])],"derivedFrom":subQ0}),makeQuery(id+"F0.imprint","IMPRINT",EDGE,{"disambiguationData":[TD([[subQ1,1.0]])],"derivedFrom":subQ0}),makeQuery(id+"F0.imprint","IMPRINT",EDGE,{"disambiguationData":[TD([[subQ1,-1.0]])],"derivedFrom":subQ0})])],"isStart":false});}
            var Q2;
            {var subQ0=sQuery(id+"F0.wireOp",EDGE,"E5");var subQ1=makeQuery(id+"F0.imprint","INTERSECT",VERTEX,{"disambiguationData":[OD(0.0)],"derivedFrom":[subQ0,sQuery(id+"F0.wireOp",EDGE,"E9")]});Q2=makeQuery(id+"F1.opExtrude","CAP_EDGE",EDGE,{"disambiguationData":[OSD([subQ0]),TDD([makeQuery(id+"F0.imprint","IMPRINT",EDGE,{"disambiguationData":[TD([[makeQuery(id+"F0.imprint","INTERSECT",VERTEX,{"derivedFrom":[subQ0,sQuery(id+"F0.wireOp",EDGE,"E19")]}),1.0]])],"derivedFrom":subQ0}),makeQuery(id+"F0.imprint","IMPRINT",EDGE,{"disambiguationData":[TD([[subQ1,1.0]])],"derivedFrom":subQ0})])],"isStart":false});}
            var Q3;
            {var subQ0=sQuery(id+"F0.wireOp",EDGE,"E2");var subQ1=makeQuery(id+"F0.imprint","INTERSECT",VERTEX,{"disambiguationData":[OD(0.0)],"derivedFrom":[subQ0,sQuery(id+"F0.wireOp",EDGE,"E16.MirrorCS")]});Q3=makeQuery(id+"F1.opExtrude","CAP_EDGE",EDGE,{"disambiguationData":[OSD([subQ0]),TDD([makeQuery(id+"F0.imprint","IMPRINT",EDGE,{"disambiguationData":[TD([[makeQuery(id+"F0.imprint","INTERSECT",VERTEX,{"disambiguationData":[OD(0.0)],"derivedFrom":[subQ0,sQuery(id+"F0.wireOp",EDGE,"E12")]}),-1.0]])],"derivedFrom":subQ0}),makeQuery(id+"F0.imprint","IMPRINT",EDGE,{"disambiguationData":[TD([[subQ1,-1.0]])],"derivedFrom":subQ0})])],"isStart":false});}
            var Q4;
            {var subQ0=sQuery(id+"F0.wireOp",EDGE,"E14");Q4=makeQuery(id+"F1.opExtrude","CAP_EDGE",EDGE,{"disambiguationData":[OSD([subQ0]),TDD([makeQuery(id+"F0.imprint","IMPRINT",EDGE,{"disambiguationData":[TD([[makeQuery(id+"F0.imprint","INTERSECT",VERTEX,{"disambiguationData":[OD(0.0)],"derivedFrom":[sQuery(id+"F0.wireOp",EDGE,"E4"),subQ0]}),-1.0]])],"derivedFrom":subQ0})])],"isStart":false});}
            var Q5;
            {var subQ0=sQuery(id+"F0.wireOp",EDGE,"E12");Q5=makeQuery(id+"F1.opExtrude","CAP_EDGE",EDGE,{"disambiguationData":[OSD([subQ0]),TDD([makeQuery(id+"F0.imprint","IMPRINT",EDGE,{"disambiguationData":[TD([[makeQuery(id+"F0.imprint","INTERSECT",VERTEX,{"disambiguationData":[OD(1.0)],"derivedFrom":[sQuery(id+"F0.wireOp",EDGE,"E2"),subQ0]}),-1.0]])],"derivedFrom":subQ0}),makeQuery(id+"F0.imprint","IMPRINT",EDGE,{"disambiguationData":[TD([[makeQuery(id+"F0.imprint","INTERSECT",VERTEX,{"disambiguationData":[OD(1.0)],"derivedFrom":[sQuery(id+"F0.wireOp",EDGE,"E5"),subQ0]}),1.0]])],"derivedFrom":subQ0})])],"isStart":false});}
            var Q6;
            {var subQ0=sQuery(id+"F0.wireOp",EDGE,"E5");Q6=makeQuery(id+"F1.opExtrude","CAP_EDGE",EDGE,{"disambiguationData":[OSD([subQ0]),TDD([makeQuery(id+"F0.imprint","IMPRINT",EDGE,{"disambiguationData":[TD([[makeQuery(id+"F0.imprint","INTERSECT",VERTEX,{"disambiguationData":[OD(1.0)],"derivedFrom":[subQ0,sQuery(id+"F0.wireOp",EDGE,"E14")]}),-1.0]])],"derivedFrom":subQ0})])],"isStart":false});}
            var Q7;
            {var subQ0=sQuery(id+"F0.wireOp",EDGE,"E14");Q7=makeQuery(id+"F1.opExtrude","CAP_EDGE",EDGE,{"disambiguationData":[OSD([subQ0]),TDD([makeQuery(id+"F0.imprint","IMPRINT",EDGE,{"disambiguationData":[TD([[makeQuery(id+"F0.imprint","INTERSECT",VERTEX,{"disambiguationData":[OD(1.0)],"derivedFrom":[sQuery(id+"F0.wireOp",EDGE,"E4"),subQ0]}),1.0]])],"derivedFrom":subQ0})])],"isStart":false});}
            var Q8;
            {var subQ0=sQuery(id+"F0.wireOp",EDGE,"E11");Q8=makeQuery(id+"F1.opExtrude","CAP_EDGE",EDGE,{"disambiguationData":[OSD([subQ0]),TDD([makeQuery(id+"F0.imprint","IMPRINT",EDGE,{"disambiguationData":[TD([[makeQuery(id+"F0.imprint","INTERSECT",VERTEX,{"disambiguationData":[OD(1.0)],"derivedFrom":[sQuery(id+"F0.wireOp",EDGE,"E5"),subQ0]}),-1.0]])],"derivedFrom":subQ0}),makeQuery(id+"F0.imprint","IMPRINT",EDGE,{"disambiguationData":[TD([[makeQuery(id+"F0.imprint","INTERSECT",VERTEX,{"disambiguationData":[OD(1.0)],"derivedFrom":[sQuery(id+"F0.wireOp",EDGE,"E2"),subQ0]}),1.0]])],"derivedFrom":subQ0})])],"isStart":false});}
            var Q9;
            {var subQ0=sQuery(id+"F0.wireOp",EDGE,"E5");var subQ1=makeQuery(id+"F0.imprint","INTERSECT",VERTEX,{"disambiguationData":[OD(1.0)],"derivedFrom":[subQ0,sQuery(id+"F0.wireOp",EDGE,"E9")]});Q9=makeQuery(id+"F1.opExtrude","CAP_EDGE",EDGE,{"disambiguationData":[OSD([subQ0]),TDD([makeQuery(id+"F0.imprint","IMPRINT",EDGE,{"disambiguationData":[TD([[makeQuery(id+"F0.imprint","INTERSECT",VERTEX,{"derivedFrom":[subQ0,sQuery(id+"F0.wireOp",EDGE,"E25.MirrorCS")]}),-1.0]])],"derivedFrom":subQ0}),makeQuery(id+"F0.imprint","IMPRINT",EDGE,{"disambiguationData":[TD([[subQ1,-1.0]])],"derivedFrom":subQ0})])],"isStart":false});}
            var Q10;
            {var subQ0=sQuery(id+"F0.wireOp",EDGE,"E26");Q10=makeQuery(id+"F1.opExtrude","CAP_EDGE",EDGE,{"disambiguationData":[OSD([subQ0]),TDD([makeQuery(id+"F0.imprint","IMPRINT",EDGE,{"disambiguationData":[TD([[makeQuery(id+"F0.imprint","INTERSECT",VERTEX,{"derivedFrom":[sQuery(id+"F0.wireOp",EDGE,"E20"),subQ0]}),1.0]])],"derivedFrom":subQ0})])],"isStart":false});}
            var Q11;
            {var subQ0=sQuery(id+"F0.wireOp",EDGE,"E2");var subQ1=makeQuery(id+"F0.imprint","INTERSECT",VERTEX,{"disambiguationData":[OD(1.0)],"derivedFrom":[subQ0,sQuery(id+"F0.wireOp",EDGE,"E14")]});var subQ2=makeQuery(id+"F0.imprint","INTERSECT",VERTEX,{"derivedFrom":[subQ0,sQuery(id+"F0.wireOp",EDGE,"E22.MirrorCS")]});var subQ3=makeQuery(id+"F0.imprint","INTERSECT",VERTEX,{"derivedFrom":[subQ0,sQuery(id+"F0.wireOp",EDGE,"E23.MirrorCS")]});var subQ4=makeQuery(id+"F0.imprint","INTERSECT",VERTEX,{"disambiguationData":[OD(1.0)],"derivedFrom":[subQ0,sQuery(id+"F0.wireOp",EDGE,"E9")]});Q11=makeQuery(id+"F1.opExtrude","CAP_EDGE",EDGE,{"disambiguationData":[OSD([subQ0]),TDD([makeQuery(id+"F0.imprint","IMPRINT",EDGE,{"disambiguationData":[TD([[makeQuery(id+"F0.imprint","INTERSECT",VERTEX,{"derivedFrom":[subQ0,sQuery(id+"F0.wireOp",EDGE,"E25.MirrorCS")]}),-1.0]])],"derivedFrom":subQ0}),makeQuery(id+"F0.imprint","IMPRINT",EDGE,{"disambiguationData":[TD([[subQ4,-1.0]])],"derivedFrom":subQ0}),makeQuery(id+"F0.imprint","IMPRINT",EDGE,{"disambiguationData":[TD([[subQ3,-1.0]])],"derivedFrom":subQ0}),makeQuery(id+"F0.imprint","IMPRINT",EDGE,{"disambiguationData":[TD([[subQ2,-1.0]])],"derivedFrom":subQ0}),makeQuery(id+"F0.imprint","IMPRINT",EDGE,{"disambiguationData":[TD([[subQ1,-1.0]])],"derivedFrom":subQ0})])],"isStart":false});}
            var Q12;
            {var subQ0=sQuery(id+"F0.wireOp",EDGE,"E4");var subQ1=makeQuery(id+"F0.imprint","INTERSECT",VERTEX,{"derivedFrom":[subQ0,sQuery(id+"F0.wireOp",EDGE,"E23.MirrorCS")]});var subQ3=makeQuery(id+"F0.imprint","INTERSECT",VERTEX,{"derivedFrom":[subQ0,sQuery(id+"F0.wireOp",EDGE,"E25.MirrorCS")]});Q12=makeQuery(id+"F1.opExtrude","CAP_EDGE",EDGE,{"disambiguationData":[OSD([subQ0]),TDD([makeQuery(id+"F0.imprint","IMPRINT",EDGE,{"disambiguationData":[TD([[makeQuery(id+"F0.imprint","INTERSECT",VERTEX,{"derivedFrom":[subQ0,sQuery(id+"F0.wireOp",EDGE,"E24.MirrorCS")]}),-1.0]])],"derivedFrom":subQ0}),makeQuery(id+"F0.imprint","IMPRINT",EDGE,{"disambiguationData":[TD([[subQ3,-1.0]])],"derivedFrom":subQ0}),makeQuery(id+"F0.imprint","IMPRINT",EDGE,{"disambiguationData":[TD([[subQ1,1.0]])],"derivedFrom":subQ0}),makeQuery(id+"F0.imprint","IMPRINT",EDGE,{"disambiguationData":[TD([[makeQuery(id+"F0.imprint","INTERSECT",VERTEX,{"derivedFrom":[subQ0,sQuery(id+"F0.wireOp",EDGE,"E22.MirrorCS")]}),1.0]])],"derivedFrom":subQ0})])],"isStart":false});}
            var Q13;
            Q13=makeQuery(id+"F1.opExtrude","CAP_EDGE",EDGE,{"disambiguationData":[OSD([sQuery(id+"F0.wireOp",EDGE,"E21")])],"isStart":false});
            var Q14;
            {var subQ0=sQuery(id+"F0.wireOp",EDGE,"E11");Q14=makeQuery(id+"F1.opExtrude","CAP_EDGE",EDGE,{"disambiguationData":[OSD([subQ0]),TDD([makeQuery(id+"F0.imprint","IMPRINT",EDGE,{"disambiguationData":[TD([[makeQuery(id+"F0.imprint","INTERSECT",VERTEX,{"disambiguationData":[OD(0.0)],"derivedFrom":[sQuery(id+"F0.wireOp",EDGE,"E2"),subQ0]}),-1.0]])],"derivedFrom":subQ0}),makeQuery(id+"F0.imprint","IMPRINT",EDGE,{"disambiguationData":[TD([[makeQuery(id+"F0.imprint","INTERSECT",VERTEX,{"disambiguationData":[OD(0.0)],"derivedFrom":[sQuery(id+"F0.wireOp",EDGE,"E5"),subQ0]}),1.0]])],"derivedFrom":subQ0})])],"isStart":false});}
            var Q15;
            Q15=makeQuery(id+"F1.opExtrude","CAP_EDGE",EDGE,{"disambiguationData":[OSD([sQuery(id+"F0.wireOp",EDGE,"E24.MirrorCS")])],"isStart":false});
            var Q16;
            Q16=makeQuery(id+"F1.opExtrude","CAP_EDGE",EDGE,{"disambiguationData":[OSD([sQuery(id+"F0.wireOp",EDGE,"E20")])],"isStart":false});
            var Q17;
            Q17=makeQuery(id+"F1.opExtrude","CAP_EDGE",EDGE,{"disambiguationData":[OSD([sQuery(id+"F0.wireOp",EDGE,"E3")])],"isStart":false});
            var Q18;
            Q18=makeQuery(id+"F1.opExtrude","CAP_EDGE",EDGE,{"disambiguationData":[OSD([sQuery(id+"F0.wireOp",EDGE,"E22.MirrorCS")])],"isStart":false});
            var Q19;
            {var subQ0=sQuery(id+"F0.wireOp",EDGE,"E2");var subQ1=makeQuery(id+"F0.imprint","INTERSECT",VERTEX,{"disambiguationData":[OD(0.0)],"derivedFrom":[subQ0,sQuery(id+"F0.wireOp",EDGE,"E14")]});Q19=makeQuery(id+"F1.opExtrude","CAP_EDGE",EDGE,{"disambiguationData":[OSD([subQ0]),TDD([makeQuery(id+"F0.imprint","IMPRINT",EDGE,{"disambiguationData":[TD([[makeQuery(id+"F0.imprint","INTERSECT",VERTEX,{"derivedFrom":[subQ0,sQuery(id+"F0.wireOp",EDGE,"E18")]}),-1.0]])],"derivedFrom":subQ0}),makeQuery(id+"F0.imprint","IMPRINT",EDGE,{"disambiguationData":[TD([[subQ1,-1.0]])],"derivedFrom":subQ0})])],"isStart":false});}
            var Q20;
            Q20=makeQuery(id+"F1.opExtrude","CAP_EDGE",EDGE,{"disambiguationData":[OSD([sQuery(id+"F0.wireOp",EDGE,"E18")])],"isStart":false});
            var Q21;
            {var subQ0=sQuery(id+"F0.wireOp",EDGE,"E5");Q21=makeQuery(id+"F1.opExtrude","CAP_EDGE",EDGE,{"disambiguationData":[OSD([subQ0]),TDD([makeQuery(id+"F0.imprint","IMPRINT",EDGE,{"disambiguationData":[TD([[makeQuery(id+"F0.imprint","INTERSECT",VERTEX,{"disambiguationData":[OD(0.0)],"derivedFrom":[subQ0,sQuery(id+"F0.wireOp",EDGE,"E14")]}),-1.0]])],"derivedFrom":subQ0})])],"isStart":false});}
            var Q22;
            {var subQ0=sQuery(id+"F0.wireOp",EDGE,"E26");Q22=makeQuery(id+"F1.opExtrude","CAP_EDGE",EDGE,{"disambiguationData":[OSD([subQ0]),TDD([makeQuery(id+"F0.imprint","IMPRINT",EDGE,{"disambiguationData":[TD([[makeQuery(id+"F0.imprint","INTERSECT",VERTEX,{"derivedFrom":[sQuery(id+"F0.wireOp",EDGE,"E22.MirrorCS"),subQ0]}),1.0]])],"derivedFrom":subQ0})])],"isStart":false});}
            var Q23;
            {var subQ0=sQuery(id+"F0.wireOp",EDGE,"E5");Q23=makeQuery(id+"F1.opExtrude","CAP_EDGE",EDGE,{"disambiguationData":[OSD([subQ0]),TDD([makeQuery(id+"F0.imprint","IMPRINT",EDGE,{"disambiguationData":[TD([[makeQuery(id+"F0.imprint","INTERSECT",VERTEX,{"disambiguationData":[OD(0.0)],"derivedFrom":[subQ0,sQuery(id+"F0.wireOp",EDGE,"E12")]}),-1.0]])],"derivedFrom":subQ0})])],"isStart":false});}
            var Q24;
            {var subQ0=sQuery(id+"F0.wireOp",EDGE,"E2");var subQ1=makeQuery(id+"F0.imprint","INTERSECT",VERTEX,{"disambiguationData":[OD(0.0)],"derivedFrom":[subQ0,sQuery(id+"F0.wireOp",EDGE,"E9")]});var subQ3=makeQuery(id+"F0.imprint","INTERSECT",VERTEX,{"derivedFrom":[subQ0,sQuery(id+"F0.wireOp",EDGE,"E21")]});var subQ4=makeQuery(id+"F0.imprint","INTERSECT",VERTEX,{"disambiguationData":[OD(1.0)],"derivedFrom":[subQ0,sQuery(id+"F0.wireOp",EDGE,"E16.MirrorCS")]});Q24=makeQuery(id+"F1.opExtrude","CAP_EDGE",EDGE,{"disambiguationData":[OSD([subQ0]),TDD([makeQuery(id+"F0.imprint","IMPRINT",EDGE,{"disambiguationData":[TD([[makeQuery(id+"F0.imprint","INTERSECT",VERTEX,{"derivedFrom":[subQ0,sQuery(id+"F0.wireOp",EDGE,"E19")]}),1.0]])],"derivedFrom":subQ0}),makeQuery(id+"F0.imprint","IMPRINT",EDGE,{"disambiguationData":[TD([[makeQuery(id+"F0.imprint","INTERSECT",VERTEX,{"disambiguationData":[OD(1.0)],"derivedFrom":[subQ0,sQuery(id+"F0.wireOp",EDGE,"E11")]}),-1.0]])],"derivedFrom":subQ0}),makeQuery(id+"F0.imprint","IMPRINT",EDGE,{"disambiguationData":[TD([[subQ4,-1.0]])],"derivedFrom":subQ0}),makeQuery(id+"F0.imprint","IMPRINT",EDGE,{"disambiguationData":[TD([[subQ3,-1.0]])],"derivedFrom":subQ0}),makeQuery(id+"F0.imprint","IMPRINT",EDGE,{"disambiguationData":[TD([[subQ1,1.0]])],"derivedFrom":subQ0})])],"isStart":false});}
            var Q25;
            {var subQ0=sQuery(id+"F0.wireOp",EDGE,"E12");Q25=makeQuery(id+"F1.opExtrude","CAP_EDGE",EDGE,{"disambiguationData":[OSD([subQ0]),TDD([makeQuery(id+"F0.imprint","IMPRINT",EDGE,{"disambiguationData":[TD([[makeQuery(id+"F0.imprint","INTERSECT",VERTEX,{"disambiguationData":[OD(0.0)],"derivedFrom":[sQuery(id+"F0.wireOp",EDGE,"E5"),subQ0]}),-1.0]])],"derivedFrom":subQ0}),makeQuery(id+"F0.imprint","IMPRINT",EDGE,{"disambiguationData":[TD([[makeQuery(id+"F0.imprint","INTERSECT",VERTEX,{"disambiguationData":[OD(0.0)],"derivedFrom":[sQuery(id+"F0.wireOp",EDGE,"E2"),subQ0]}),1.0]])],"derivedFrom":subQ0})])],"isStart":false});}
            var Q26;
            {var subQ0=sQuery(id+"F0.wireOp",EDGE,"E5");Q26=makeQuery(id+"F1.opExtrude","CAP_EDGE",EDGE,{"disambiguationData":[OSD([subQ0]),TDD([makeQuery(id+"F0.imprint","IMPRINT",EDGE,{"disambiguationData":[TD([[makeQuery(id+"F0.imprint","INTERSECT",VERTEX,{"disambiguationData":[OD(1.0)],"derivedFrom":[subQ0,sQuery(id+"F0.wireOp",EDGE,"E11")]}),-1.0]])],"derivedFrom":subQ0})])],"isStart":false});}
            var Q27;
            {var subQ0=sQuery(id+"F0.wireOp",EDGE,"E4");var subQ1=makeQuery(id+"F0.imprint","INTERSECT",VERTEX,{"disambiguationData":[OD(1.0)],"derivedFrom":[subQ0,sQuery(id+"F0.wireOp",EDGE,"E11")]});var subQ2=makeQuery(id+"F0.imprint","INTERSECT",VERTEX,{"disambiguationData":[OD(1.0)],"derivedFrom":[subQ0,sQuery(id+"F0.wireOp",EDGE,"E12")]});Q27=makeQuery(id+"F1.opExtrude","CAP_EDGE",EDGE,{"disambiguationData":[OSD([subQ0]),TDD([makeQuery(id+"F0.imprint","IMPRINT",EDGE,{"disambiguationData":[TD([[makeQuery(id+"F0.imprint","INTERSECT",VERTEX,{"disambiguationData":[OD(1.0)],"derivedFrom":[subQ0,sQuery(id+"F0.wireOp",EDGE,"E14")]}),-1.0]])],"derivedFrom":subQ0}),makeQuery(id+"F0.imprint","IMPRINT",EDGE,{"disambiguationData":[TD([[subQ2,-1.0]])],"derivedFrom":subQ0}),makeQuery(id+"F0.imprint","IMPRINT",EDGE,{"disambiguationData":[TD([[subQ1,-1.0]])],"derivedFrom":subQ0})])],"isStart":false});}
            var Q28;
            {var subQ0=sQuery(id+"F0.wireOp",EDGE,"E4");var subQ1=makeQuery(id+"F0.imprint","INTERSECT",VERTEX,{"disambiguationData":[OD(0.0)],"derivedFrom":[subQ0,sQuery(id+"F0.wireOp",EDGE,"E12")]});var subQ2=makeQuery(id+"F0.imprint","INTERSECT",VERTEX,{"disambiguationData":[OD(0.0)],"derivedFrom":[subQ0,sQuery(id+"F0.wireOp",EDGE,"E11")]});Q28=makeQuery(id+"F1.opExtrude","CAP_EDGE",EDGE,{"disambiguationData":[OSD([subQ0]),TDD([makeQuery(id+"F0.imprint","IMPRINT",EDGE,{"disambiguationData":[TD([[makeQuery(id+"F0.imprint","INTERSECT",VERTEX,{"disambiguationData":[OD(0.0)],"derivedFrom":[subQ0,sQuery(id+"F0.wireOp",EDGE,"E14")]}),-1.0]])],"derivedFrom":subQ0}),makeQuery(id+"F0.imprint","IMPRINT",EDGE,{"disambiguationData":[TD([[subQ2,-1.0]])],"derivedFrom":subQ0}),makeQuery(id+"F0.imprint","IMPRINT",EDGE,{"disambiguationData":[TD([[subQ1,-1.0]])],"derivedFrom":subQ0})])],"isStart":false});}
            var Q29;
            {var subQ0=sQuery(id+"F0.wireOp",EDGE,"E16.MirrorCS");Q29=makeQuery(id+"F1.opExtrude","CAP_EDGE",EDGE,{"disambiguationData":[OSD([subQ0]),TDD([makeQuery(id+"F0.imprint","IMPRINT",EDGE,{"disambiguationData":[TD([[makeQuery(id+"F0.imprint","INTERSECT",VERTEX,{"disambiguationData":[OD(1.0)],"derivedFrom":[sQuery(id+"F0.wireOp",EDGE,"E4"),subQ0]}),1.0]])],"derivedFrom":subQ0})])],"isStart":false});}
            var Q30;
            Q30=makeQuery(id+"F1.opExtrude","CAP_EDGE",EDGE,{"disambiguationData":[OSD([sQuery(id+"F0.wireOp",EDGE,"E23.MirrorCS")])],"isStart":false});
            fillet(context, id + "F4", {"entities" : qUnion([Q0, Q1, Q2, Q3, Q4, Q5, Q6, Q7, Q8, Q9, Q10, Q11, Q12, Q13, Q14, Q15, Q16, Q17, Q18, Q19, Q20, Q21, Q22, Q23, Q24, Q25, Q26, Q27, Q28, Q29, Q30]), "radius" : 2.54 * mm, "tangentPropagation" : true, "allowEdgeOverflow" : false});
        }
    });
